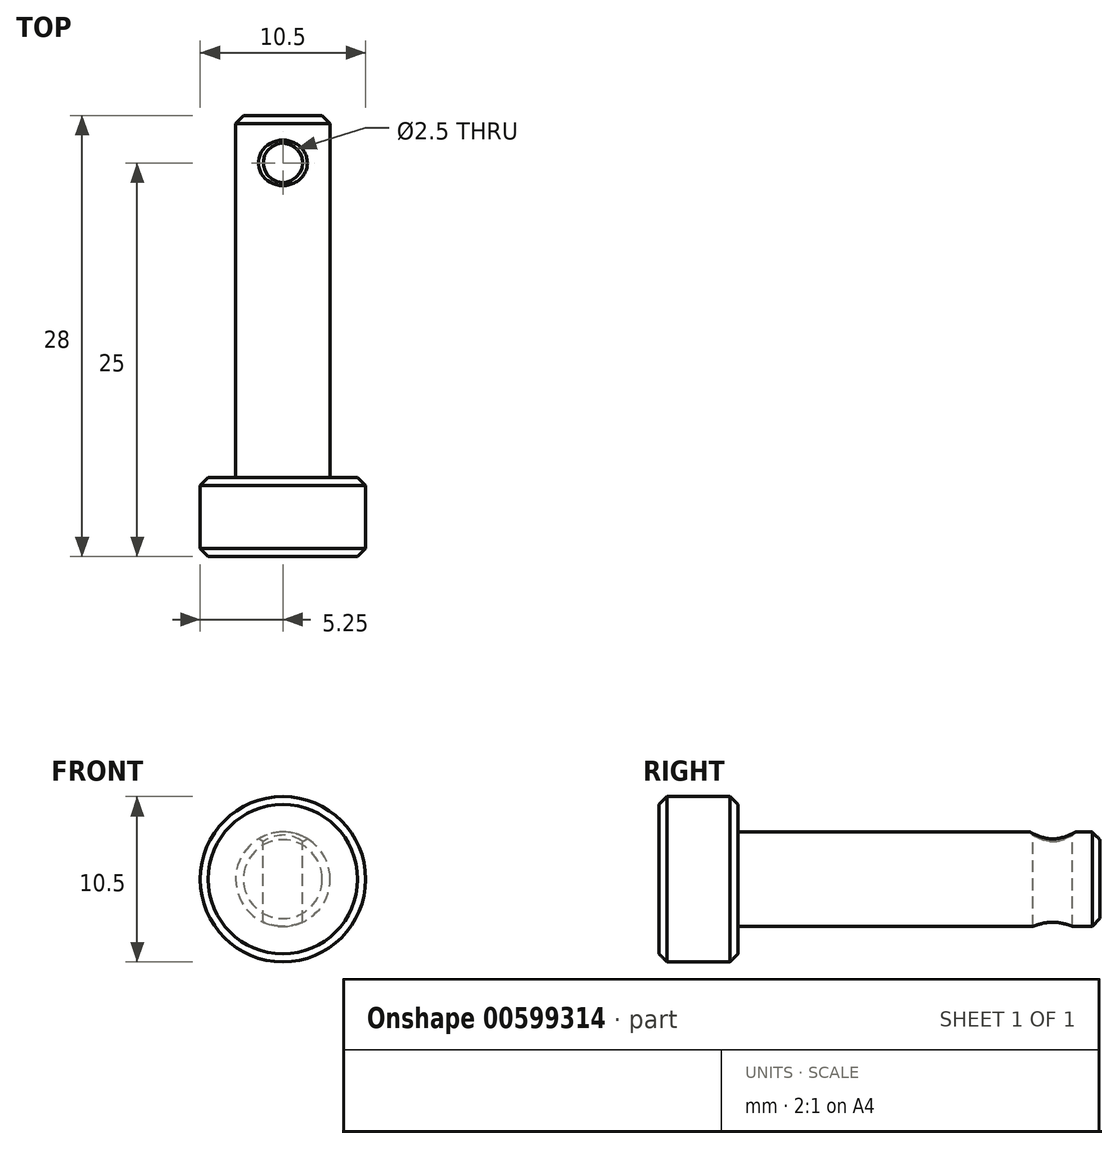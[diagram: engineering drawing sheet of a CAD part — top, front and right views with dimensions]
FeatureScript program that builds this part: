
annotation { "Feature Type Name" : "Feature", "Feature Type Description" : "" }
export const myFeature = defineFeature(function(context is Context, id is Id, definition is map)
    precondition{}
    {
        {
            var Q0;
            Q0=qCreatedBy(makeId("Front.planeOp"),FACE);
            var sketch = newSketch(context, id + "F0", { "sketchPlane" : qUnion([Q0])});
            skCircle(sketch, "E0", {"center": v(0, 0) * mm, "radius": 5.25 * mm});
            skSolve(sketch);
        }
        {
            var Q0;
            Q0=makeQuery(id+"F0.imprint","IMPRINT",FACE,{"disambiguationData":[TD([[makeQuery(id+"F0.imprint","IMPRINT",EDGE,{"derivedFrom":sQuery(id+"F0.wireOp",EDGE,"E0")}),1.0]])]});
            extrude(context, id + "F1", {"entities" : qUnion([Q0]), "depth" : 5 * mm, "offsetDistance" : 25 * mm});
        }
        {
            var Q0;
            Q0=makeQuery(id+"F1.opExtrude","CAP_FACE",FACE,{"disambiguationData":[OSD([sQuery(id+"F0.wireOp",EDGE,"E0")])],"isStart":true});
            var sketch = newSketch(context, id + "F2", { "sketchPlane" : qUnion([Q0])});
            skCircle(sketch, "E1", {"center": v(0, 0) * mm, "radius": 3 * mm});
            skSolve(sketch);
        }
        {
            var Q0;
            Q0=makeQuery(id+"F2.imprint","IMPRINT",FACE,{"disambiguationData":[TD([[makeQuery(id+"F2.imprint","IMPRINT",EDGE,{"derivedFrom":sQuery(id+"F2.wireOp",EDGE,"E1")}),1.0]])]});
            extrude(context, id + "F3", {"entities" : qUnion([Q0]), "operationType" : NewBodyOperationType.ADD, "depth" : 23 * mm, "offsetDistance" : 25 * mm});
        }
        {
            var Q0;
            Q0=qCreatedBy(makeId("Top.planeOp"),FACE);
            var sketch = newSketch(context, id + "F4", { "sketchPlane" : qUnion([Q0])});
            skLineSegment(sketch, "E2", {"start": v(0, 0) * mm, "end": v(0, 20) * mm, "construction": true});
            skCircle(sketch, "E3", {"center": v(0, 20) * mm, "radius": 1.25 * mm});
            skSolve(sketch);
        }
        {
            var Q0;
            Q0 = qSketchRegion(id + "F4", true);
            var Q1;
            Q1=sQuery(id+"F4.wireOp",EDGE,"E3");
            extrude(context, id + "F5", {"entities" : qUnion([Q0]), "operationType" : NewBodyOperationType.REMOVE, "surfaceEntities" : qUnion([Q1]), "endBound" : BoundingType.SYMMETRIC, "oppositeDirection" : true, "depth" : 25 * mm, "offsetDistance" : 25 * mm});
        }
        {
            var Q0;
            Q0=makeQuery(id+"F3.opExtrude","CAP_EDGE",EDGE,{"disambiguationData":[OSD([sQuery(id+"F2.wireOp",EDGE,"E1")])],"isStart":false});
            var Q1;
            Q1=makeQuery(id+"F1.opExtrude","SWEPT_FACE",FACE,{"disambiguationData":[OSD([sQuery(id+"F0.wireOp",EDGE,"E0")])]});
            chamfer(context, id + "F6", {"entities" : qUnion([Q0, Q1]), "width" : .5 * mm, "tangentPropagation" : true});
        }
        {
            var Q0;
            Q0=makeQuery(id+"F5.boolean.opBoolean","INTERSECT",EDGE,{"disambiguationData":[OD(1.0)],"derivedFrom":[makeQuery(id+"F3.opExtrude","SWEPT_FACE",FACE,{"disambiguationData":[OSD([sQuery(id+"F2.wireOp",EDGE,"E1")])]}),makeQuery(id+"F5.opExtrude","SWEPT_FACE",FACE,{"disambiguationData":[OSD([sQuery(id+"F4.wireOp",EDGE,"E3")])]})]});
            chamfer(context, id + "F7", {"entities" : qUnion([Q0]), "width" : .2 * mm, "tangentPropagation" : true});
        }
    });
